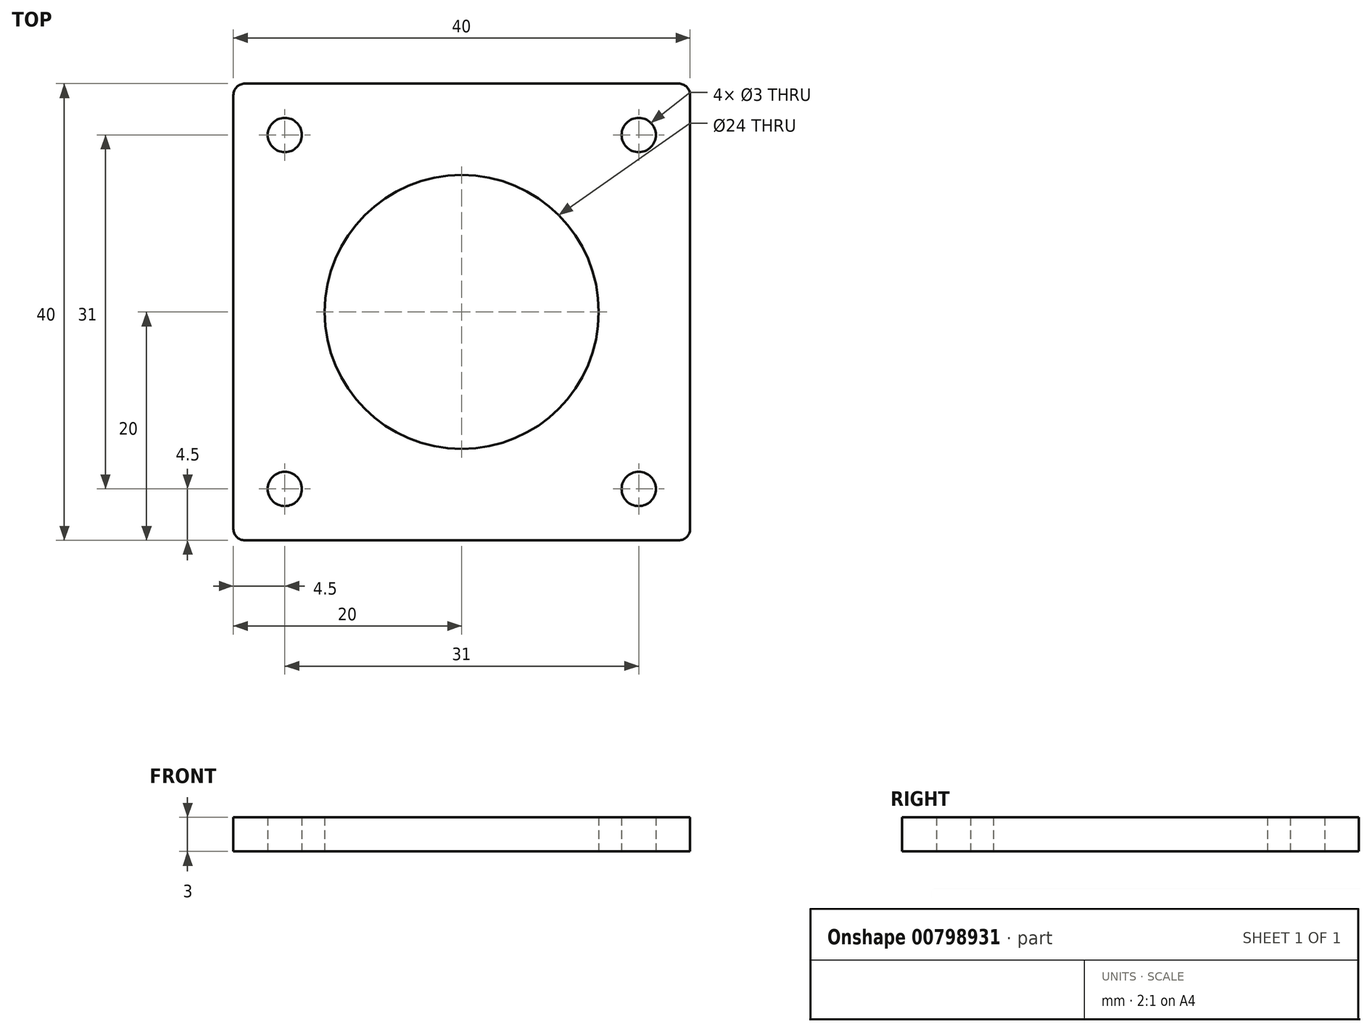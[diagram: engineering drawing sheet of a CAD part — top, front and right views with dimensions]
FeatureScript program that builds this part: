
annotation { "Feature Type Name" : "Feature", "Feature Type Description" : "" }
export const myFeature = defineFeature(function(context is Context, id is Id, definition is map)
    precondition{}
    {
        {
            var Q0;
            Q0=qCreatedBy(makeId("Top.planeOp"),FACE);
            var sketch = newSketch(context, id + "F0", { "sketchPlane" : qUnion([Q0])});
            skLineSegment(sketch, "E0.bottom", {"start": v(-19, 20) * mm, "end": v(19, 20) * mm});
            skLineSegment(sketch, "E0.top", {"start": v(-19, -20) * mm, "end": v(19, -20) * mm});
            skLineSegment(sketch, "E0.left", {"start": v(-20, 19) * mm, "end": v(-20, -19) * mm});
            skLineSegment(sketch, "E0.right", {"start": v(20, 19) * mm, "end": v(20, -19) * mm});
            skPoint(sketch, "E0.middle", {"position": v(0, 0) * mm});
            skCircle(sketch, "E1", {"center": v(-15.5, 15.5) * mm, "radius": 1.5 * mm});
            skCircle(sketch, "E2", {"center": v(15.5, 15.5) * mm, "radius": 1.5 * mm});
            skCircle(sketch, "E3", {"center": v(-15.5, -15.5) * mm, "radius": 1.5 * mm});
            skCircle(sketch, "E4", {"center": v(15.5, -15.5) * mm, "radius": 1.5 * mm});
            skPoint(sketch, "E5.visualSharp", {"position": v(-20, 20) * mm});
            skArc(sketch, "E5.filletArc", {"start": v(-19, 20) * mm, "mid": v(-19.7, 19.7) * mm, "end": v(-20, 19) * mm});
            skPoint(sketch, "E6.visualSharp", {"position": v(20, 20) * mm});
            skArc(sketch, "E6.filletArc", {"start": v(20, 19) * mm, "mid": v(19.7, 19.7) * mm, "end": v(19, 20) * mm});
            skPoint(sketch, "E7.visualSharp", {"position": v(-20, -20) * mm});
            skArc(sketch, "E7.filletArc", {"start": v(-20, -19) * mm, "mid": v(-19.7, -19.7) * mm, "end": v(-19, -20) * mm});
            skPoint(sketch, "E8.visualSharp", {"position": v(20, -20) * mm});
            skArc(sketch, "E8.filletArc", {"start": v(19, -20) * mm, "mid": v(19.7, -19.7) * mm, "end": v(20, -19) * mm});
            skCircle(sketch, "E9", {"center": v(0, 0) * mm, "radius": 12 * mm});
            skSolve(sketch);
        }
        {
            var Q0;
            Q0 = qSketchRegion(id + "F0", true);
            extrude(context, id + "F1", {"entities" : qUnion([Q0]), "depth" : 3 * mm, "offsetDistance" : 25 * mm});
        }
    });
